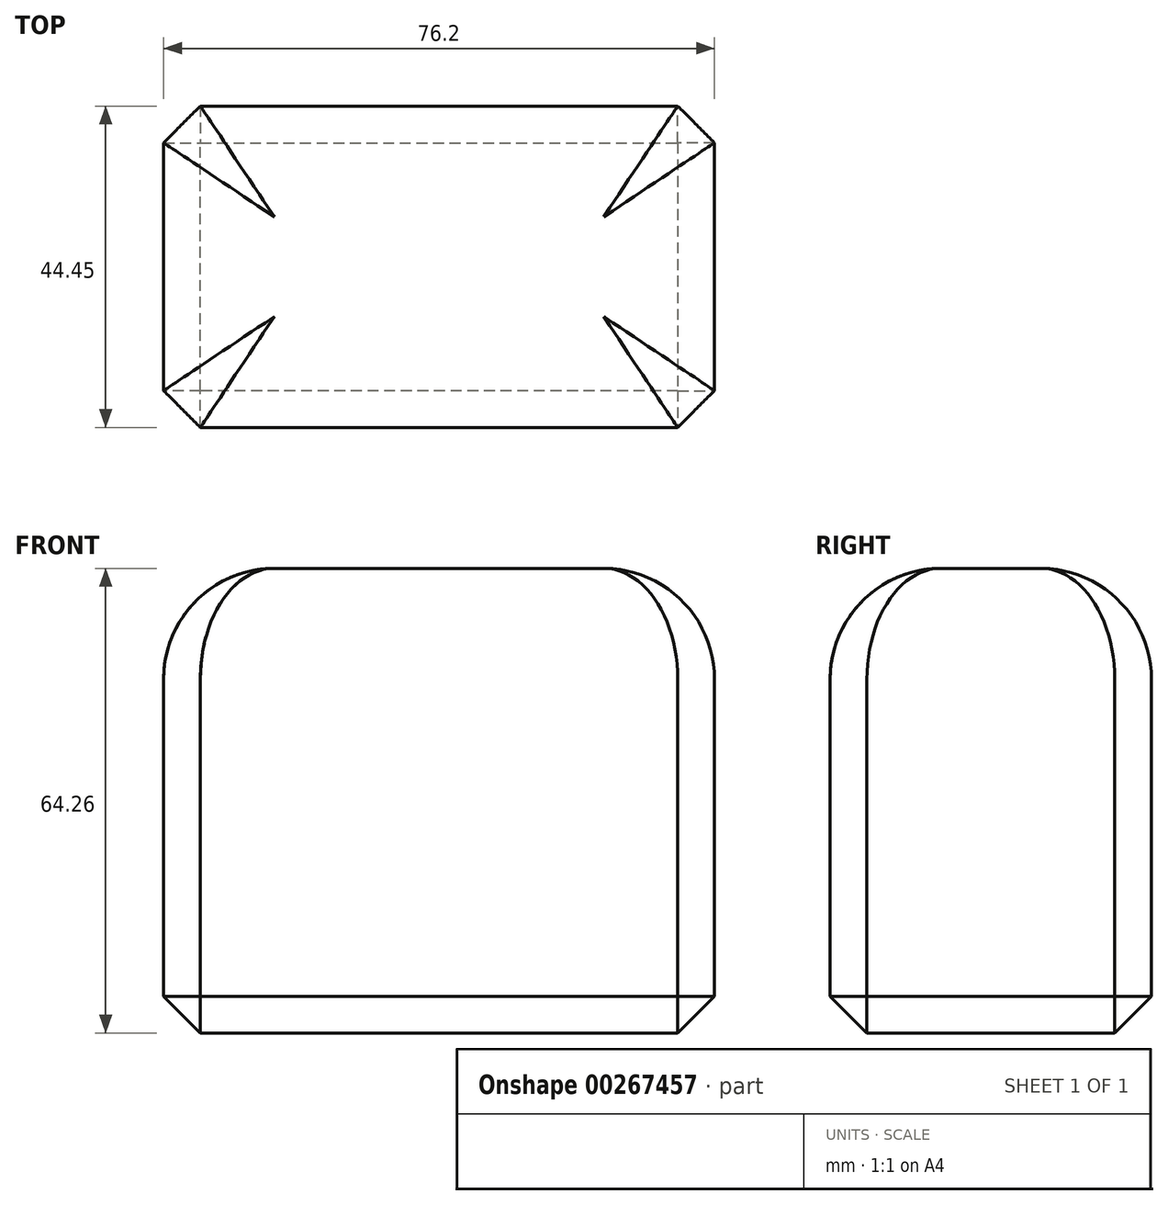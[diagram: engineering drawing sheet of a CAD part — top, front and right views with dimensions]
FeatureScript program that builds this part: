
annotation { "Feature Type Name" : "Feature", "Feature Type Description" : "" }
export const myFeature = defineFeature(function(context is Context, id is Id, definition is map)
    precondition{}
    {
        {
            var Q0;
            Q0=qCreatedBy(makeId("Top.planeOp"),FACE);
            var sketch = newSketch(context, id + "F0", { "sketchPlane" : qUnion([Q0])});
            skLineSegment(sketch, "E0.bottom", {"start": v(-18.43, 21.78) * mm, "end": v(57.77, 21.78) * mm});
            skLineSegment(sketch, "E0.top", {"start": v(-18.43, -22.67) * mm, "end": v(57.77, -22.67) * mm});
            skLineSegment(sketch, "E0.left", {"start": v(-18.43, 21.78) * mm, "end": v(-18.43, -22.67) * mm});
            skLineSegment(sketch, "E0.right", {"start": v(57.77, 21.78) * mm, "end": v(57.77, -22.67) * mm});
            skSolve(sketch);
        }
        {
            var Q0;
            Q0 = qSketchRegion(id + "F0", true);
            extrude(context, id + "F1", {"entities" : qUnion([Q0]), "depth" : 64.26 * mm});
        }
        {
            var Q0;
            Q0=makeQuery(id+"F1.opExtrude","CAP_EDGE",EDGE,{"disambiguationData":[OSD([sQuery(id+"F0.wireOp",EDGE,"E0.left")])],"isStart":false});
            var Q1;
            Q1=makeQuery(id+"F1.opExtrude","CAP_EDGE",EDGE,{"disambiguationData":[OSD([sQuery(id+"F0.wireOp",EDGE,"E0.top")])],"isStart":false});
            var Q2;
            Q2=makeQuery(id+"F1.opExtrude","CAP_FACE",FACE,{"disambiguationData":[OSD([sQuery(id+"F0.wireOp",EDGE,"E0.bottom"),sQuery(id+"F0.wireOp",EDGE,"E0.top"),sQuery(id+"F0.wireOp",EDGE,"E0.left"),sQuery(id+"F0.wireOp",EDGE,"E0.right")])],"isStart":false});
            fillet(context, id + "F2", {"entities" : qUnion([Q0, Q1, Q2]), "radius" : 15.33 * mm, "tangentPropagation" : true, "allowEdgeOverflow" : false});
        }
        {
            var Q0;
            Q0=makeQuery(id+"F1.opExtrude","SWEPT_EDGE",EDGE,{"disambiguationData":[OSD([sQuery(id+"F0.wireOp",EDGE,"E0.top"),sQuery(id+"F0.wireOp",EDGE,"E0.right")])]});
            var Q1;
            Q1=makeQuery(id+"F1.opExtrude","SWEPT_EDGE",EDGE,{"disambiguationData":[OSD([sQuery(id+"F0.wireOp",EDGE,"E0.bottom"),sQuery(id+"F0.wireOp",EDGE,"E0.right")])]});
            var Q2;
            Q2=makeQuery(id+"F1.opExtrude","SWEPT_EDGE",EDGE,{"disambiguationData":[OSD([sQuery(id+"F0.wireOp",EDGE,"E0.bottom"),sQuery(id+"F0.wireOp",EDGE,"E0.left")])]});
            var Q3;
            Q3=makeQuery(id+"F1.opExtrude","SWEPT_EDGE",EDGE,{"disambiguationData":[OSD([sQuery(id+"F0.wireOp",EDGE,"E0.top"),sQuery(id+"F0.wireOp",EDGE,"E0.left")])]});
            var Q4;
            Q4=makeQuery(id+"F1.opExtrude","CAP_EDGE",EDGE,{"disambiguationData":[OSD([sQuery(id+"F0.wireOp",EDGE,"E0.left")])],"isStart":true});
            var Q5;
            Q5=makeQuery(id+"F1.opExtrude","SWEPT_FACE",FACE,{"disambiguationData":[OSD([sQuery(id+"F0.wireOp",EDGE,"E0.bottom")])]});
            var Q6;
            Q6=makeQuery(id+"F1.opExtrude","CAP_EDGE",EDGE,{"disambiguationData":[OSD([sQuery(id+"F0.wireOp",EDGE,"E0.top")])],"isStart":true});
            var Q7;
            Q7=makeQuery(id+"F1.opExtrude","CAP_EDGE",EDGE,{"disambiguationData":[OSD([sQuery(id+"F0.wireOp",EDGE,"E0.right")])],"isStart":true});
            var Q8;
            {var subQ0=sQuery(id+"F0.wireOp",EDGE,"E0.right");Q8=makeQuery(id+"F2.opFillet","BLEND_EDGE",EDGE,{"blendedFrom":[makeQuery(id+"F1.opExtrude","CAP_EDGE",EDGE,{"disambiguationData":[OSD([subQ0])],"isStart":false}),makeQuery(id+"F1.opExtrude","CAP_FACE",FACE,{"disambiguationData":[OSD([sQuery(id+"F0.wireOp",EDGE,"E0.bottom"),sQuery(id+"F0.wireOp",EDGE,"E0.top"),sQuery(id+"F0.wireOp",EDGE,"E0.left"),subQ0])],"isStart":false})],"blendedInto":[makeQuery(id+"F1.opExtrude","CAP_FACE",FACE,{"disambiguationData":[OSD([sQuery(id+"F0.wireOp",EDGE,"E0.bottom"),sQuery(id+"F0.wireOp",EDGE,"E0.top"),sQuery(id+"F0.wireOp",EDGE,"E0.left"),subQ0])],"isStart":false})]});}
            var Q9;
            {var subQ0=sQuery(id+"F0.wireOp",EDGE,"E0.right");Q9=makeQuery(id+"F2.opFillet","BLEND_EDGE",EDGE,{"blendedFrom":[makeQuery(id+"F1.opExtrude","CAP_EDGE",EDGE,{"disambiguationData":[OSD([subQ0])],"isStart":false}),makeQuery(id+"F1.opExtrude","SWEPT_FACE",FACE,{"disambiguationData":[OSD([subQ0])]})],"blendedInto":[makeQuery(id+"F1.opExtrude","SWEPT_FACE",FACE,{"disambiguationData":[OSD([subQ0])]})]});}
            var Q10;
            Q10=makeQuery(id+"F2.opFillet","BLEND_EDGE",EDGE,{"blendedFrom":[makeQuery(id+"F1.opExtrude","CAP_EDGE",EDGE,{"disambiguationData":[OSD([sQuery(id+"F0.wireOp",EDGE,"E0.top")])],"isStart":false}),makeQuery(id+"F1.opExtrude","CAP_EDGE",EDGE,{"disambiguationData":[OSD([sQuery(id+"F0.wireOp",EDGE,"E0.right")])],"isStart":false})],"blendedInto":[]});
            var Q11;
            Q11=makeQuery(id+"F2.opFillet","BLEND_EDGE",EDGE,{"blendedFrom":[makeQuery(id+"F1.opExtrude","CAP_EDGE",EDGE,{"disambiguationData":[OSD([sQuery(id+"F0.wireOp",EDGE,"E0.bottom")])],"isStart":false}),makeQuery(id+"F1.opExtrude","CAP_EDGE",EDGE,{"disambiguationData":[OSD([sQuery(id+"F0.wireOp",EDGE,"E0.right")])],"isStart":false})],"blendedInto":[]});
            var Q12;
            {var subQ0=sQuery(id+"F0.wireOp",EDGE,"E0.bottom");Q12=makeQuery(id+"F2.opFillet","BLEND_EDGE",EDGE,{"blendedFrom":[makeQuery(id+"F1.opExtrude","CAP_EDGE",EDGE,{"disambiguationData":[OSD([subQ0])],"isStart":false}),makeQuery(id+"F1.opExtrude","CAP_FACE",FACE,{"disambiguationData":[OSD([subQ0,sQuery(id+"F0.wireOp",EDGE,"E0.top"),sQuery(id+"F0.wireOp",EDGE,"E0.left"),sQuery(id+"F0.wireOp",EDGE,"E0.right")])],"isStart":false})],"blendedInto":[makeQuery(id+"F1.opExtrude","CAP_FACE",FACE,{"disambiguationData":[OSD([subQ0,sQuery(id+"F0.wireOp",EDGE,"E0.top"),sQuery(id+"F0.wireOp",EDGE,"E0.left"),sQuery(id+"F0.wireOp",EDGE,"E0.right")])],"isStart":false})]});}
            var Q13;
            Q13=makeQuery(id+"F2.opFillet","BLEND_EDGE",EDGE,{"blendedFrom":[makeQuery(id+"F1.opExtrude","CAP_EDGE",EDGE,{"disambiguationData":[OSD([sQuery(id+"F0.wireOp",EDGE,"E0.bottom")])],"isStart":false}),makeQuery(id+"F1.opExtrude","CAP_EDGE",EDGE,{"disambiguationData":[OSD([sQuery(id+"F0.wireOp",EDGE,"E0.left")])],"isStart":false})],"blendedInto":[]});
            var Q14;
            {var subQ0=sQuery(id+"F0.wireOp",EDGE,"E0.top");Q14=makeQuery(id+"F2.opFillet","BLEND_EDGE",EDGE,{"blendedFrom":[makeQuery(id+"F1.opExtrude","CAP_EDGE",EDGE,{"disambiguationData":[OSD([subQ0])],"isStart":false}),makeQuery(id+"F1.opExtrude","CAP_FACE",FACE,{"disambiguationData":[OSD([sQuery(id+"F0.wireOp",EDGE,"E0.bottom"),subQ0,sQuery(id+"F0.wireOp",EDGE,"E0.left"),sQuery(id+"F0.wireOp",EDGE,"E0.right")])],"isStart":false})],"blendedInto":[makeQuery(id+"F1.opExtrude","CAP_FACE",FACE,{"disambiguationData":[OSD([sQuery(id+"F0.wireOp",EDGE,"E0.bottom"),subQ0,sQuery(id+"F0.wireOp",EDGE,"E0.left"),sQuery(id+"F0.wireOp",EDGE,"E0.right")])],"isStart":false})]});}
            var Q15;
            {var subQ0=sQuery(id+"F0.wireOp",EDGE,"E0.left");Q15=makeQuery(id+"F2.opFillet","BLEND_EDGE",EDGE,{"blendedFrom":[makeQuery(id+"F1.opExtrude","CAP_EDGE",EDGE,{"disambiguationData":[OSD([subQ0])],"isStart":false}),makeQuery(id+"F1.opExtrude","CAP_FACE",FACE,{"disambiguationData":[OSD([sQuery(id+"F0.wireOp",EDGE,"E0.bottom"),sQuery(id+"F0.wireOp",EDGE,"E0.top"),subQ0,sQuery(id+"F0.wireOp",EDGE,"E0.right")])],"isStart":false})],"blendedInto":[makeQuery(id+"F1.opExtrude","CAP_FACE",FACE,{"disambiguationData":[OSD([sQuery(id+"F0.wireOp",EDGE,"E0.bottom"),sQuery(id+"F0.wireOp",EDGE,"E0.top"),subQ0,sQuery(id+"F0.wireOp",EDGE,"E0.right")])],"isStart":false})]});}
            chamfer(context, id + "F3", {"entities" : qUnion([Q0, Q1, Q2, Q3, Q4, Q5, Q6, Q7, Q8, Q9, Q10, Q11, Q12, Q13, Q14, Q15]), "width" : 5.08 * mm, "tangentPropagation" : true});
        }
    });
